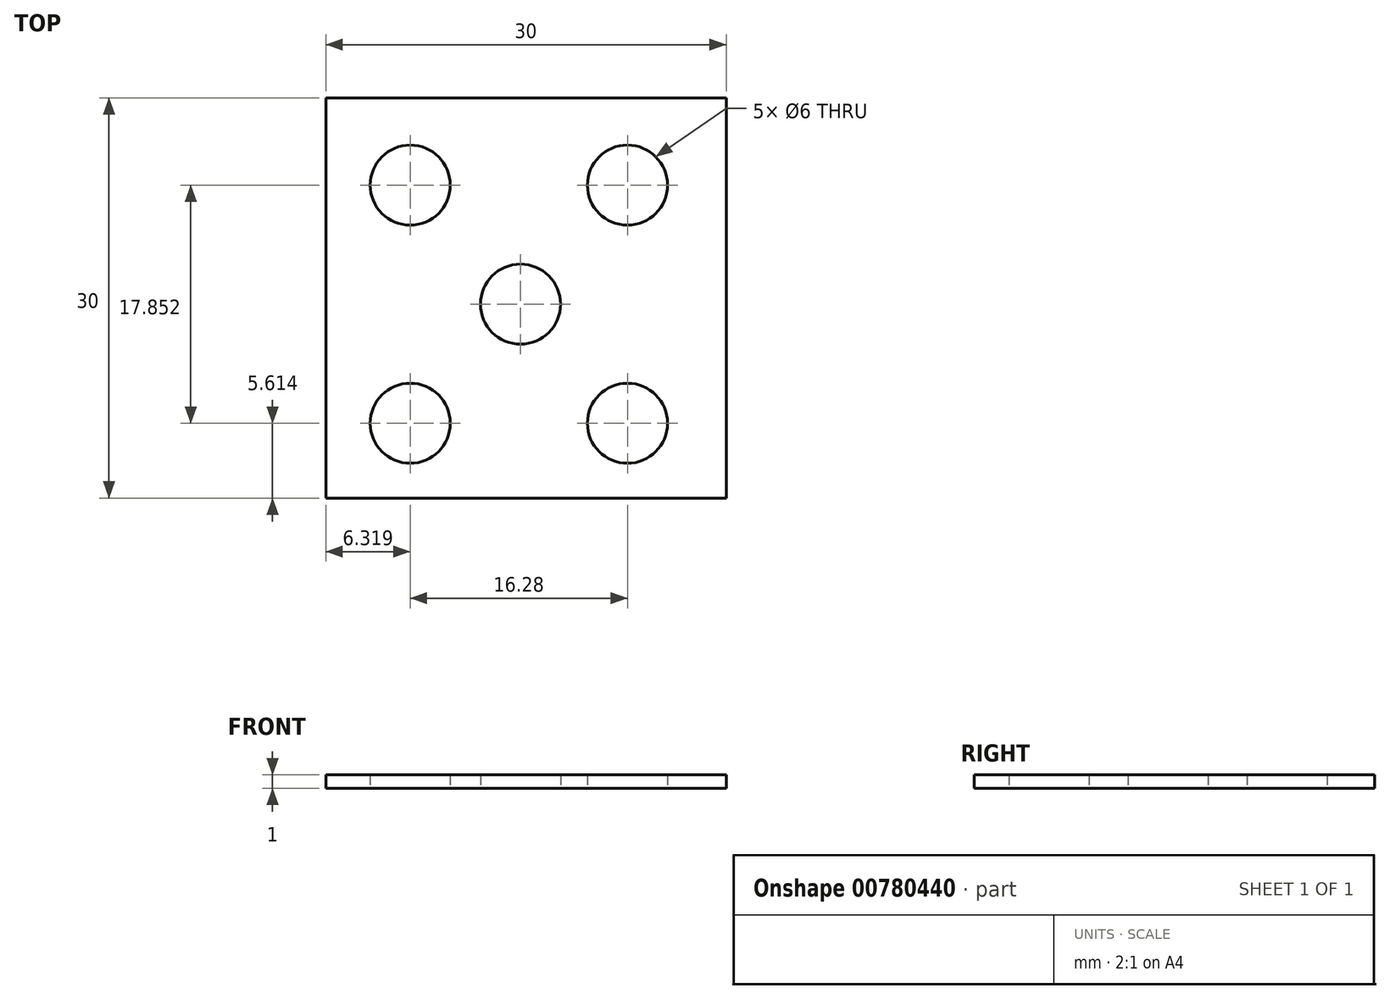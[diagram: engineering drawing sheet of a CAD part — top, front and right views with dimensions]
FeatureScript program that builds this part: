
annotation { "Feature Type Name" : "Feature", "Feature Type Description" : "" }
export const myFeature = defineFeature(function(context is Context, id is Id, definition is map)
    precondition{}
    {
        {
            var Q0;
            Q0=qCreatedBy(makeId("Top.planeOp"),FACE);
            var sketch = newSketch(context, id + "F0", { "sketchPlane" : qUnion([Q0])});
            skLineSegment(sketch, "E0.bottom", {"start": v(0, 0) * mm, "end": v(30, 0) * mm});
            skLineSegment(sketch, "E0.top", {"start": v(0, 30) * mm, "end": v(30, 30) * mm});
            skLineSegment(sketch, "E0.left", {"start": v(0, 0) * mm, "end": v(0, 30) * mm});
            skLineSegment(sketch, "E0.right", {"start": v(30, 0) * mm, "end": v(30, 30) * mm});
            skCircle(sketch, "E1", {"center": v(6.32, 23.47) * mm, "radius": 3 * mm});
            skCircle(sketch, "E2", {"center": v(6.32, 5.61) * mm, "radius": 3 * mm});
            skCircle(sketch, "E3", {"center": v(22.6, 5.61) * mm, "radius": 3 * mm});
            skCircle(sketch, "E4", {"center": v(22.6, 23.47) * mm, "radius": 3 * mm});
            skCircle(sketch, "E5", {"center": v(14.59, 14.54) * mm, "radius": 3 * mm});
            skSolve(sketch);
        }
        {
            var Q0;
            Q0 = qSketchRegion(id + "F0", true);
            extrude(context, id + "F1", {"entities" : qUnion([Q0]), "depth" : 1 * mm, "offsetDistance" : 25 * mm});
        }
    });
